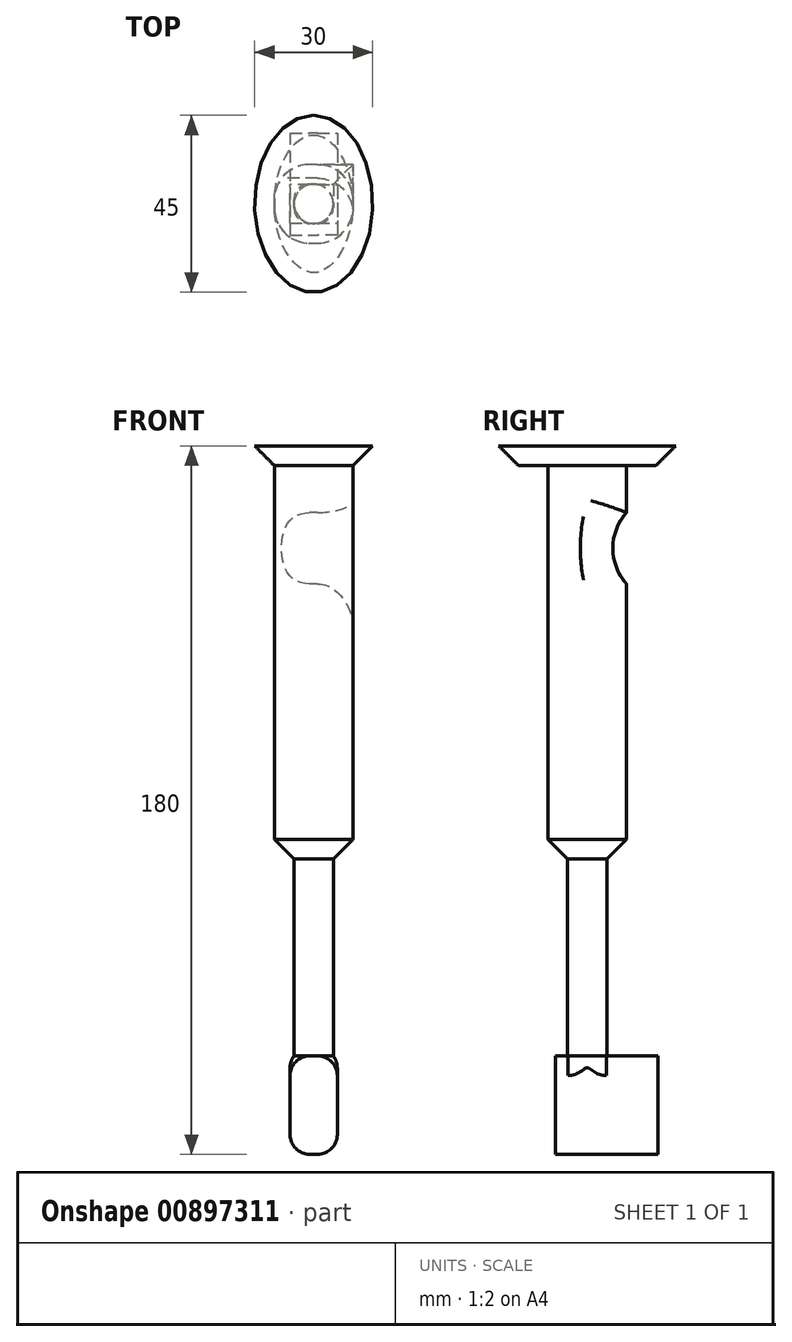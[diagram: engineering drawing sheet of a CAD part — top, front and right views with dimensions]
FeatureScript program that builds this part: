
annotation { "Feature Type Name" : "Feature", "Feature Type Description" : "" }
export const myFeature = defineFeature(function(context is Context, id is Id, definition is map)
    precondition{}
    {
        {
            var Q0;
            Q0=qCreatedBy(makeId("Top.planeOp"),FACE);
            var sketch = newSketch(context, id + "F0", { "sketchPlane" : qUnion([Q0])});
            skEllipse(sketch, "E0", {"center": v(0, 0) * mm, "majorRadius": 22.5 * mm, "minorRadius": 15 * mm, "majorAxis": v(0, 1)});
            skSolve(sketch);
        }
        {
            var Q0;
            Q0=makeQuery(id+"F0.imprint","IMPRINT",FACE,{"disambiguationData":[TD([[makeQuery(id+"F0.imprint","IMPRINT",EDGE,{"derivedFrom":sQuery(id+"F0.wireOp",EDGE,"E0")}),1.0]])]});
            extrude(context, id + "F1", {"entities" : qUnion([Q0]), "depth" : 5 * mm, "offsetDistance" : 25 * mm});
        }
        {
            var Q0;
            Q0=makeQuery(id+"F1.opExtrude","CAP_FACE",FACE,{"disambiguationData":[OSD([sQuery(id+"F0.wireOp",EDGE,"E0")])],"isStart":true});
            var sketch = newSketch(context, id + "F2", { "sketchPlane" : qUnion([Q0])});
            skLineSegment(sketch, "E1.bottom", {"start": v(-10, -10) * mm, "end": v(10, -10) * mm});
            skLineSegment(sketch, "E1.top", {"start": v(-10, 10) * mm, "end": v(10, 10) * mm});
            skLineSegment(sketch, "E1.left", {"start": v(-10, -10) * mm, "end": v(-10, 10) * mm});
            skLineSegment(sketch, "E1.right", {"start": v(10, -10) * mm, "end": v(10, 10) * mm});
            skPoint(sketch, "E1.middle", {"position": v(0, 0) * mm});
            skSolve(sketch);
        }
        {
            var Q0;
            Q0=makeQuery(id+"F2.imprint","IMPRINT",FACE,{"disambiguationData":[TD([[makeQuery(id+"F2.imprint","IMPRINT",EDGE,{"derivedFrom":sQuery(id+"F2.wireOp",EDGE,"E1.bottom")}),1.0]])]});
            extrude(context, id + "F3", {"entities" : qUnion([Q0]), "operationType" : NewBodyOperationType.ADD, "depth" : 100 * mm, "offsetDistance" : 25 * mm});
        }
        {
            var Q0;
            Q0=makeQuery(id+"F3.opExtrude","SWEPT_FACE",FACE,{"disambiguationData":[OSD([sQuery(id+"F2.wireOp",EDGE,"E1.left")])]});
            var sketch = newSketch(context, id + "F4", { "sketchPlane" : qUnion([Q0])});
            skLineSegment(sketch, "E2", {"start": v(-10, -100) * mm, "end": v(-20, -100) * mm});
            skLineSegment(sketch, "E3", {"start": v(-20, -100) * mm, "end": v(-20, -75) * mm});
            skCircle(sketch, "E4", {"center": v(-20, -75) * mm, "radius": 13.5 * mm});
            skLineSegment(sketch, "E5", {"start": v(-20, -75) * mm, "end": v(-20, -48) * mm});
            skCircle(sketch, "E6", {"center": v(-20, -48) * mm, "radius": 13.5 * mm});
            skLineSegment(sketch, "E7", {"start": v(-20, -48) * mm, "end": v(-20, -21) * mm});
            skCircle(sketch, "E8", {"center": v(-20, -21) * mm, "radius": 13.5 * mm});
            skSolve(sketch);
        }
        {
            var Q0;
            {var subQ0=sQuery(id+"F4.wireOp",EDGE,"E4");var subQ1=makeQuery(id+"F3.opExtrude","SWEPT_EDGE",EDGE,{"disambiguationData":[OSD([sQuery(id+"F2.wireOp",EDGE,"E1.bottom"),sQuery(id+"F2.wireOp",EDGE,"E1.left")])]});var subQ2=makeQuery(id+"F4.imprint","INTERSECT",VERTEX,{"disambiguationData":[OD(0.0)],"derivedFrom":[subQ1,subQ0]});Q0=makeQuery(id+"F4.imprint","IMPRINT",FACE,{"disambiguationData":[TD([[makeQuery(id+"F4.imprint","IMPRINT",EDGE,{"disambiguationData":[TD([[subQ2,1.0]])],"derivedFrom":subQ0}),1.0]])]});}
            var Q1;
            {var subQ0=sQuery(id+"F4.wireOp",EDGE,"E6");var subQ1=makeQuery(id+"F3.opExtrude","SWEPT_EDGE",EDGE,{"disambiguationData":[OSD([sQuery(id+"F2.wireOp",EDGE,"E1.bottom"),sQuery(id+"F2.wireOp",EDGE,"E1.left")])]});var subQ2=makeQuery(id+"F4.imprint","INTERSECT",VERTEX,{"disambiguationData":[OD(0.0)],"derivedFrom":[subQ1,subQ0]});Q1=makeQuery(id+"F4.imprint","IMPRINT",FACE,{"disambiguationData":[TD([[makeQuery(id+"F4.imprint","IMPRINT",EDGE,{"disambiguationData":[TD([[subQ2,1.0]])],"derivedFrom":subQ0}),1.0]])]});}
            var Q2;
            {var subQ0=sQuery(id+"F4.wireOp",EDGE,"E8");var subQ1=makeQuery(id+"F3.opExtrude","SWEPT_EDGE",EDGE,{"disambiguationData":[OSD([sQuery(id+"F2.wireOp",EDGE,"E1.bottom"),sQuery(id+"F2.wireOp",EDGE,"E1.left")])]});var subQ2=makeQuery(id+"F4.imprint","INTERSECT",VERTEX,{"disambiguationData":[OD(0.0)],"derivedFrom":[subQ1,subQ0]});Q2=makeQuery(id+"F4.imprint","IMPRINT",FACE,{"disambiguationData":[TD([[makeQuery(id+"F4.imprint","IMPRINT",EDGE,{"disambiguationData":[TD([[subQ2,1.0]])],"derivedFrom":subQ0}),1.0]])]});}
            extrude(context, id + "F5", {"entities" : qUnion([Q0, Q1, Q2]), "operationType" : NewBodyOperationType.REMOVE, "oppositeDirection" : true, "depth" : 45.1 * mm, "offsetDistance" : 25 * mm});
        }
        {
            var Q0;
            Q0=makeQuery(id+"F3.opExtrude","SWEPT_EDGE",EDGE,{"disambiguationData":[OSD([sQuery(id+"F2.wireOp",EDGE,"E1.top"),sQuery(id+"F2.wireOp",EDGE,"E1.left")])]});
            var Q1;
            Q1=makeQuery(id+"F3.opExtrude","SWEPT_EDGE",EDGE,{"disambiguationData":[OSD([sQuery(id+"F2.wireOp",EDGE,"E1.top"),sQuery(id+"F2.wireOp",EDGE,"E1.right")])]});
            var Q2;
            {var subQ0=sQuery(id+"F2.wireOp",EDGE,"E1.bottom");var subQ1=sQuery(id+"F2.wireOp",EDGE,"E1.right");Q2=makeQuery(id+"F5.boolean.opBoolean","SPLIT",EDGE,{"disambiguationData":[TD([makeQuery(id+"F3.opExtrude","SWEPT_FACE",FACE,{"disambiguationData":[OSD([subQ0])]}),makeQuery(id+"F3.opExtrude","CAP_FACE",FACE,{"disambiguationData":[OSD([subQ0,sQuery(id+"F2.wireOp",EDGE,"E1.top"),sQuery(id+"F2.wireOp",EDGE,"E1.left"),subQ1])],"isStart":false}),makeQuery(id+"F3.opExtrude","SWEPT_FACE",FACE,{"disambiguationData":[OSD([subQ1])]}),makeQuery(id+"F5.opExtrude","SWEPT_FACE",FACE,{"disambiguationData":[OSD([sQuery(id+"F4.wireOp",EDGE,"E4")])]})])],"derivedFrom":makeQuery(id+"F3.opExtrude","SWEPT_EDGE",EDGE,{"disambiguationData":[OSD([subQ0,subQ1])]})});}
            var Q3;
            {var subQ0=sQuery(id+"F2.wireOp",EDGE,"E1.bottom");var subQ1=sQuery(id+"F2.wireOp",EDGE,"E1.right");Q3=makeQuery(id+"F5.boolean.opBoolean","SPLIT",EDGE,{"disambiguationData":[TD([makeQuery(id+"F3.opExtrude","SWEPT_FACE",FACE,{"disambiguationData":[OSD([subQ0])]}),makeQuery(id+"F3.opExtrude","SWEPT_FACE",FACE,{"disambiguationData":[OSD([subQ1])]}),makeQuery(id+"F5.opExtrude","SWEPT_FACE",FACE,{"disambiguationData":[OSD([sQuery(id+"F4.wireOp",EDGE,"E4")])]}),makeQuery(id+"F5.opExtrude","SWEPT_FACE",FACE,{"disambiguationData":[OSD([sQuery(id+"F4.wireOp",EDGE,"E6")])]})])],"derivedFrom":makeQuery(id+"F3.opExtrude","SWEPT_EDGE",EDGE,{"disambiguationData":[OSD([subQ0,subQ1])]})});}
            var Q4;
            {var subQ0=sQuery(id+"F2.wireOp",EDGE,"E1.bottom");var subQ1=sQuery(id+"F2.wireOp",EDGE,"E1.right");Q4=makeQuery(id+"F5.boolean.opBoolean","SPLIT",EDGE,{"disambiguationData":[TD([makeQuery(id+"F3.opExtrude","SWEPT_FACE",FACE,{"disambiguationData":[OSD([subQ0])]}),makeQuery(id+"F3.opExtrude","SWEPT_FACE",FACE,{"disambiguationData":[OSD([subQ1])]}),makeQuery(id+"F5.opExtrude","SWEPT_FACE",FACE,{"disambiguationData":[OSD([sQuery(id+"F4.wireOp",EDGE,"E6")])]}),makeQuery(id+"F5.opExtrude","SWEPT_FACE",FACE,{"disambiguationData":[OSD([sQuery(id+"F4.wireOp",EDGE,"E8")])]})])],"derivedFrom":makeQuery(id+"F3.opExtrude","SWEPT_EDGE",EDGE,{"disambiguationData":[OSD([subQ0,subQ1])]})});}
            var Q5;
            {var subQ0=sQuery(id+"F2.wireOp",EDGE,"E1.bottom");var subQ1=sQuery(id+"F2.wireOp",EDGE,"E1.right");Q5=makeQuery(id+"F5.boolean.opBoolean","SPLIT",EDGE,{"disambiguationData":[TD([makeQuery(id+"F1.opExtrude","CAP_FACE",FACE,{"disambiguationData":[OSD([sQuery(id+"F0.wireOp",EDGE,"E0")])],"isStart":true}),makeQuery(id+"F3.opExtrude","SWEPT_FACE",FACE,{"disambiguationData":[OSD([subQ0])]}),makeQuery(id+"F3.opExtrude","SWEPT_FACE",FACE,{"disambiguationData":[OSD([subQ1])]}),makeQuery(id+"F5.opExtrude","SWEPT_FACE",FACE,{"disambiguationData":[OSD([sQuery(id+"F4.wireOp",EDGE,"E8")])]})])],"derivedFrom":makeQuery(id+"F3.opExtrude","SWEPT_EDGE",EDGE,{"disambiguationData":[OSD([subQ0,subQ1])]})});}
            var Q6;
            Q6=makeQuery(id+"F5.boolean.opBoolean","INTERSECT",EDGE,{"derivedFrom":[makeQuery(id+"F3.opExtrude","SWEPT_FACE",FACE,{"disambiguationData":[OSD([sQuery(id+"F2.wireOp",EDGE,"E1.right")])]}),makeQuery(id+"F5.opExtrude","SWEPT_FACE",FACE,{"disambiguationData":[OSD([sQuery(id+"F4.wireOp",EDGE,"E8")])]})]});
            var Q7;
            Q7=makeQuery(id+"F5.boolean.opBoolean","INTERSECT",EDGE,{"derivedFrom":[makeQuery(id+"F3.opExtrude","SWEPT_FACE",FACE,{"disambiguationData":[OSD([sQuery(id+"F2.wireOp",EDGE,"E1.right")])]}),makeQuery(id+"F5.opExtrude","SWEPT_FACE",FACE,{"disambiguationData":[OSD([sQuery(id+"F4.wireOp",EDGE,"E6")])]})]});
            var Q8;
            Q8=makeQuery(id+"F5.boolean.opBoolean","INTERSECT",EDGE,{"derivedFrom":[makeQuery(id+"F3.opExtrude","SWEPT_FACE",FACE,{"disambiguationData":[OSD([sQuery(id+"F2.wireOp",EDGE,"E1.right")])]}),makeQuery(id+"F5.opExtrude","SWEPT_FACE",FACE,{"disambiguationData":[OSD([sQuery(id+"F4.wireOp",EDGE,"E4")])]})]});
            var Q9;
            Q9=makeQuery(id+"F5.boolean.opBoolean","COPY",EDGE,{"derivedFrom":makeQuery(id+"F5.opExtrude","CAP_EDGE",EDGE,{"disambiguationData":[OSD([sQuery(id+"F4.wireOp",EDGE,"E4")])],"isStart":true})});
            var Q10;
            {var subQ0=sQuery(id+"F2.wireOp",EDGE,"E1.bottom");var subQ1=sQuery(id+"F2.wireOp",EDGE,"E1.left");Q10=makeQuery(id+"F5.boolean.opBoolean","SPLIT",EDGE,{"disambiguationData":[TD([makeQuery(id+"F3.opExtrude","SWEPT_FACE",FACE,{"disambiguationData":[OSD([subQ0])]}),makeQuery(id+"F3.opExtrude","CAP_FACE",FACE,{"disambiguationData":[OSD([subQ0,sQuery(id+"F2.wireOp",EDGE,"E1.top"),subQ1,sQuery(id+"F2.wireOp",EDGE,"E1.right")])],"isStart":false}),makeQuery(id+"F3.opExtrude","SWEPT_FACE",FACE,{"disambiguationData":[OSD([subQ1])]}),makeQuery(id+"F5.opExtrude","SWEPT_FACE",FACE,{"disambiguationData":[OSD([sQuery(id+"F4.wireOp",EDGE,"E4")])]})])],"derivedFrom":makeQuery(id+"F3.opExtrude","SWEPT_EDGE",EDGE,{"disambiguationData":[OSD([subQ0,subQ1])]})});}
            var Q11;
            Q11=makeQuery(id+"F5.boolean.opBoolean","COPY",EDGE,{"derivedFrom":makeQuery(id+"F5.opExtrude","CAP_EDGE",EDGE,{"disambiguationData":[OSD([sQuery(id+"F4.wireOp",EDGE,"E6")])],"isStart":true})});
            var Q12;
            Q12=makeQuery(id+"F5.boolean.opBoolean","COPY",EDGE,{"derivedFrom":makeQuery(id+"F5.opExtrude","CAP_EDGE",EDGE,{"disambiguationData":[OSD([sQuery(id+"F4.wireOp",EDGE,"E8")])],"isStart":true})});
            var Q13;
            {var subQ0=sQuery(id+"F2.wireOp",EDGE,"E1.bottom");var subQ1=sQuery(id+"F2.wireOp",EDGE,"E1.left");Q13=makeQuery(id+"F5.boolean.opBoolean","SPLIT",EDGE,{"disambiguationData":[TD([makeQuery(id+"F1.opExtrude","CAP_FACE",FACE,{"disambiguationData":[OSD([sQuery(id+"F0.wireOp",EDGE,"E0")])],"isStart":true}),makeQuery(id+"F3.opExtrude","SWEPT_FACE",FACE,{"disambiguationData":[OSD([subQ0])]}),makeQuery(id+"F3.opExtrude","SWEPT_FACE",FACE,{"disambiguationData":[OSD([subQ1])]}),makeQuery(id+"F5.opExtrude","SWEPT_FACE",FACE,{"disambiguationData":[OSD([sQuery(id+"F4.wireOp",EDGE,"E8")])]})])],"derivedFrom":makeQuery(id+"F3.opExtrude","SWEPT_EDGE",EDGE,{"disambiguationData":[OSD([subQ0,subQ1])]})});}
            fillet(context, id + "F6", {"entities" : qUnion([Q0, Q1, Q2, Q3, Q4, Q5, Q6, Q7, Q8, Q9, Q10, Q11, Q12, Q13]), "radius" : 9 * mm, "tangentPropagation" : true, "allowEdgeOverflow" : false});
        }
        {
            var Q0;
            Q0=makeQuery(id+"F3.opExtrude","CAP_FACE",FACE,{"disambiguationData":[OSD([sQuery(id+"F2.wireOp",EDGE,"E1.bottom"),sQuery(id+"F2.wireOp",EDGE,"E1.top"),sQuery(id+"F2.wireOp",EDGE,"E1.left"),sQuery(id+"F2.wireOp",EDGE,"E1.right")])],"isStart":false});
            var sketch = newSketch(context, id + "F7", { "sketchPlane" : qUnion([Q0])});
            skCircle(sketch, "E9", {"center": v(0, 0) * mm, "radius": 5 * mm});
            skSolve(sketch);
        }
        {
            var Q0;
            Q0=makeQuery(id+"F7.imprint","IMPRINT",FACE,{"disambiguationData":[TD([[makeQuery(id+"F7.imprint","IMPRINT",EDGE,{"derivedFrom":sQuery(id+"F7.wireOp",EDGE,"E9")}),1.0]])]});
            extrude(context, id + "F8", {"entities" : qUnion([Q0]), "operationType" : NewBodyOperationType.ADD, "depth" : 50 * mm, "offsetDistance" : 25 * mm});
        }
        {
            var Q0;
            {var subQ0=sQuery(id+"F2.wireOp",EDGE,"E1.left");var subQ1=sQuery(id+"F2.wireOp",EDGE,"E1.top");Q0=makeQuery(id+"F6.opFillet","BLEND_EDGE",EDGE,{"blendedFrom":[makeQuery(id+"F3.opExtrude","SWEPT_EDGE",EDGE,{"disambiguationData":[OSD([subQ1,subQ0])]}),makeQuery(id+"F3.opExtrude","CAP_FACE",FACE,{"disambiguationData":[OSD([sQuery(id+"F2.wireOp",EDGE,"E1.bottom"),subQ1,subQ0,sQuery(id+"F2.wireOp",EDGE,"E1.right")])],"isStart":false})],"blendedInto":[makeQuery(id+"F3.opExtrude","CAP_FACE",FACE,{"disambiguationData":[OSD([sQuery(id+"F2.wireOp",EDGE,"E1.bottom"),subQ1,subQ0,sQuery(id+"F2.wireOp",EDGE,"E1.right")])],"isStart":false})]});}
            chamfer(context, id + "F9", {"entities" : qUnion([Q0]), "width" : 5 * mm, "tangentPropagation" : true});
        }
        {
            var Q0;
            Q0=makeQuery(id+"F1.opExtrude","CAP_EDGE",EDGE,{"disambiguationData":[OSD([sQuery(id+"F0.wireOp",EDGE,"E0")])],"isStart":true});
            chamfer(context, id + "F10", {"entities" : qUnion([Q0]), "width" : 5 * mm, "tangentPropagation" : true});
        }
        {
            var Q0;
            Q0=makeQuery(id+"F8.opExtrude","CAP_FACE",FACE,{"disambiguationData":[OSD([sQuery(id+"F7.wireOp",EDGE,"E9")])],"isStart":false});
            var sketch = newSketch(context, id + "F11", { "sketchPlane" : qUnion([Q0])});
            skLineSegment(sketch, "E10.bottom", {"start": v(6, -18) * mm, "end": v(-6, -18) * mm});
            skLineSegment(sketch, "E10.top", {"start": v(6, 18) * mm, "end": v(-6, 18) * mm});
            skLineSegment(sketch, "E10.left", {"start": v(6, -18) * mm, "end": v(6, 18) * mm});
            skLineSegment(sketch, "E10.right", {"start": v(-6, -18) * mm, "end": v(-6, 18) * mm});
            skPoint(sketch, "E10.middle", {"position": v(0, 0) * mm});
            skSolve(sketch);
        }
        {
            var Q0;
            Q0=makeQuery(id+"F11.imprint","IMPRINT",FACE,{"disambiguationData":[TD([[makeQuery(id+"F11.imprint","IMPRINT",EDGE,{"derivedFrom":sQuery(id+"F11.wireOp",EDGE,"E10.bottom")}),-1.0]])]});
            var Q1;
            Q1=makeQuery(id+"F11.imprint","IMPRINT",FACE,{"disambiguationData":[TD([[makeQuery(id+"F11.imprint","IMPRINT",EDGE,{"derivedFrom":makeQuery(id+"F8.opExtrude","CAP_EDGE",EDGE,{"disambiguationData":[OSD([sQuery(id+"F7.wireOp",EDGE,"E9")])],"isStart":false})}),1.0]])]});
            extrude(context, id + "F12", {"entities" : qUnion([Q0, Q1]), "operationType" : NewBodyOperationType.ADD, "depth" : 25 * mm, "offsetDistance" : 25 * mm});
        }
        {
            var Q0;
            Q0=makeQuery(id+"F12.opExtrude","CAP_FACE",FACE,{"disambiguationData":[OSD([sQuery(id+"F11.wireOp",EDGE,"E10.bottom"),sQuery(id+"F11.wireOp",EDGE,"E10.top"),sQuery(id+"F11.wireOp",EDGE,"E10.left"),sQuery(id+"F11.wireOp",EDGE,"E10.right")])],"isStart":false});
            var sketch = newSketch(context, id + "F13", { "sketchPlane" : qUnion([Q0])});
            skLineSegment(sketch, "E11", {"start": v(0, -18) * mm, "end": v(0, 8) * mm});
            skLineSegment(sketch, "E12", {"start": v(0, 8) * mm, "end": v(6, 8) * mm});
            skLineSegment(sketch, "E13", {"start": v(6, 8) * mm, "end": v(6, 18) * mm});
            skLineSegment(sketch, "E14", {"start": v(6, 18) * mm, "end": v(-6, 18) * mm});
            skLineSegment(sketch, "E15", {"start": v(-6, 18) * mm, "end": v(-6, 8) * mm});
            skLineSegment(sketch, "E16", {"start": v(-6, 8) * mm, "end": v(0, 8) * mm});
            skSolve(sketch);
        }
        {
            var Q0;
            Q0=makeQuery(id+"F13.imprint","IMPRINT",FACE,{"disambiguationData":[TD([[makeQuery(id+"F13.imprint","IMPRINT",EDGE,{"derivedFrom":sQuery(id+"F13.wireOp",EDGE,"E12")}),1.0]])]});
            extrude(context, id + "F14", {"entities" : qUnion([Q0]), "operationType" : NewBodyOperationType.REMOVE, "oppositeDirection" : true, "depth" : 25 * mm, "offsetDistance" : 25 * mm});
        }
        {
            var Q0;
            Q0=makeQuery(id+"F14.boolean.opBoolean","COPY",EDGE,{"derivedFrom":makeQuery(id+"F14.opExtrude","SWEPT_EDGE",EDGE,{"disambiguationData":[OSD([sQuery(id+"F11.wireOp",EDGE,"E10.right"),sQuery(id+"F13.wireOp",EDGE,"E15"),sQuery(id+"F13.wireOp",EDGE,"E16")])]})});
            var Q1;
            Q1=makeQuery(id+"F14.boolean.opBoolean","COPY",EDGE,{"derivedFrom":makeQuery(id+"F14.opExtrude","SWEPT_EDGE",EDGE,{"disambiguationData":[OSD([sQuery(id+"F11.wireOp",EDGE,"E10.left"),sQuery(id+"F13.wireOp",EDGE,"E12"),sQuery(id+"F13.wireOp",EDGE,"E13")])]})});
            var Q2;
            Q2=makeQuery(id+"F12.opExtrude","CAP_EDGE",EDGE,{"disambiguationData":[OSD([sQuery(id+"F11.wireOp",EDGE,"E10.right")])],"isStart":false});
            var Q3;
            Q3=makeQuery(id+"F12.opExtrude","CAP_EDGE",EDGE,{"disambiguationData":[OSD([sQuery(id+"F11.wireOp",EDGE,"E10.left")])],"isStart":false});
            var Q4;
            Q4=makeQuery(id+"F12.opExtrude","CAP_EDGE",EDGE,{"disambiguationData":[OSD([sQuery(id+"F11.wireOp",EDGE,"E10.left")])],"isStart":true});
            var Q5;
            Q5=makeQuery(id+"F12.opExtrude","CAP_EDGE",EDGE,{"disambiguationData":[OSD([sQuery(id+"F11.wireOp",EDGE,"E10.right")])],"isStart":true});
            fillet(context, id + "F15", {"entities" : qUnion([Q0, Q1, Q2, Q3, Q4, Q5]), "radius" : 5 * mm, "tangentPropagation" : true, "allowEdgeOverflow" : false});
        }
    });
